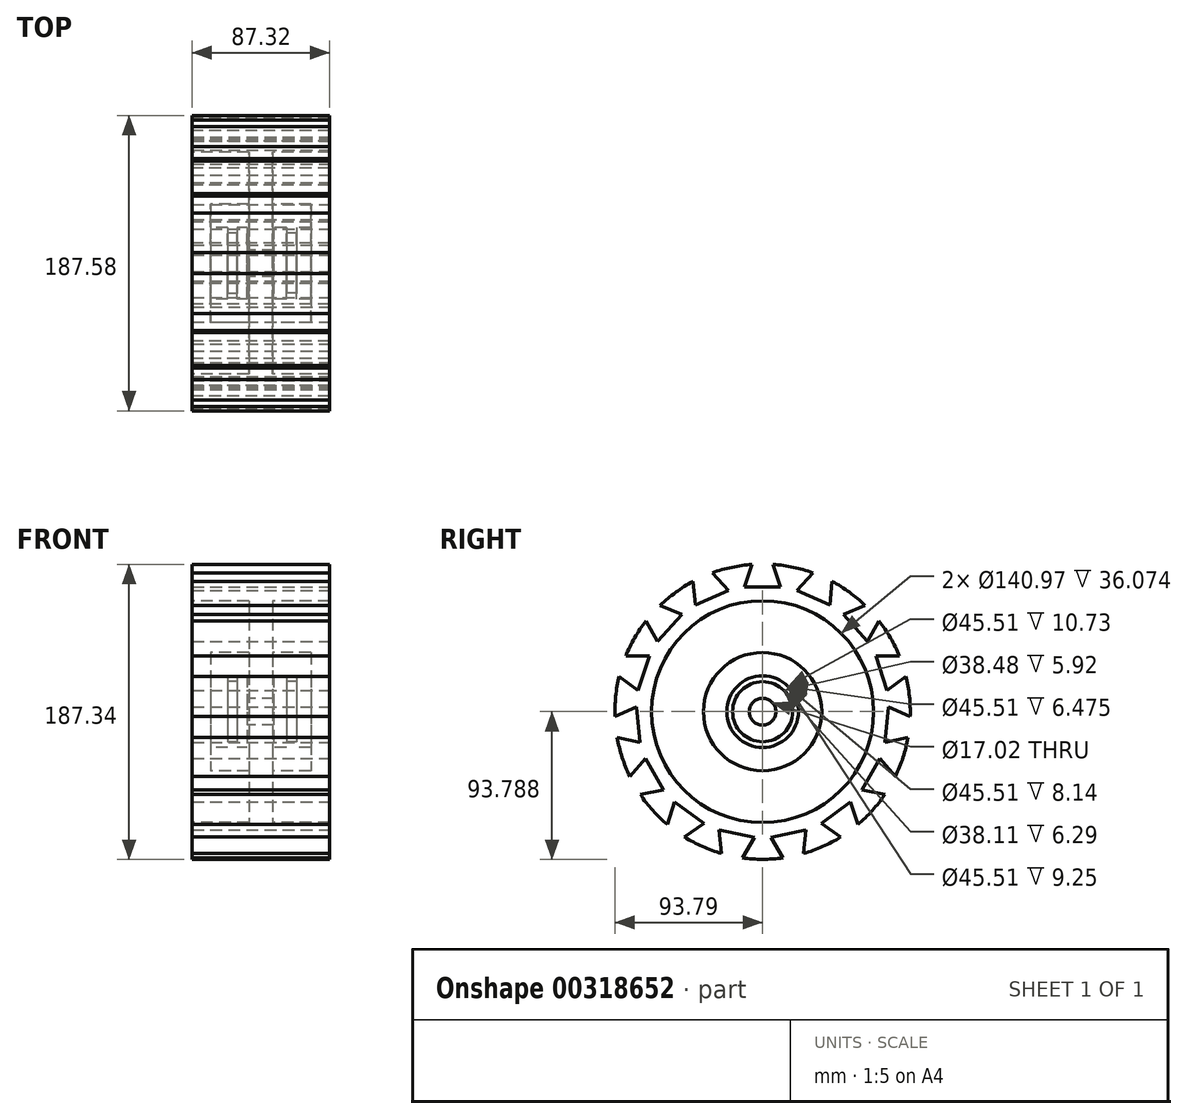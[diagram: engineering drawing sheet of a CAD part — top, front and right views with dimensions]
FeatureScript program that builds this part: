
annotation { "Feature Type Name" : "Feature", "Feature Type Description" : "" }
export const myFeature = defineFeature(function(context is Context, id is Id, definition is map)
    precondition{}
    {
        {
            var Q0;
            Q0=qCreatedBy(makeId("Front.planeOp"),FACE);
            var sketch = newSketch(context, id + "F0", { "sketchPlane" : qUnion([Q0])});
            skLineSegment(sketch, "E0.bottom", {"start": v(-43.66, 44.12) * mm, "end": v(-7.58, 44.12) * mm});
            skLineSegment(sketch, "E0.top", {"start": v(-43.66, 67.43) * mm, "end": v(43.66, 67.43) * mm});
            skLineSegment(sketch, "E0.left", {"start": v(-43.66, 44.12) * mm, "end": v(-43.66, 67.43) * mm});
            skLineSegment(sketch, "E0.right", {"start": v(43.66, 44.12) * mm, "end": v(43.66, 67.43) * mm});
            skPoint(sketch, "E0.middle", {"position": v(0, 55.78) * mm});
            skLineSegment(sketch, "E1.left", {"start": v(-7.58, 44.12) * mm, "end": v(-7.58, 11.2) * mm});
            skLineSegment(sketch, "E1.right", {"start": v(7.58, 44.12) * mm, "end": v(7.58, 11.2) * mm});
            skPoint(sketch, "E1.middle", {"position": v(0, 27.66) * mm});
            skLineSegment(sketch, "E2.bottom", {"start": v(-31.82, 11.2) * mm, "end": v(-7.58, 11.2) * mm});
            skLineSegment(sketch, "E2.top", {"start": v(-31.82, -3.6) * mm, "end": v(-21.09, -3.6) * mm});
            skLineSegment(sketch, "E2.left", {"start": v(-31.82, 11.2) * mm, "end": v(-31.82, -3.6) * mm});
            skLineSegment(sketch, "E2.right", {"start": v(31.82, 11.2) * mm, "end": v(31.82, -3.6) * mm});
            skPoint(sketch, "E2.middle", {"position": v(0, 3.8) * mm});
            skPoint(sketch, "E2.middle.positionSnap0", {"position": v(0, 11.2) * mm});
            skPoint(sketch, "E2.cornerSnap0", {"position": v(0, 11.2) * mm});
            skPoint(sketch, "E2.centerSnap0", {"position": v(0, 11.2) * mm});
            skLineSegment(sketch, "E3.top", {"start": v(-21.09, -7.12) * mm, "end": v(-15.17, -7.12) * mm});
            skLineSegment(sketch, "E3.left", {"start": v(-21.09, -3.6) * mm, "end": v(-21.09, -7.12) * mm});
            skLineSegment(sketch, "E3.right", {"start": v(-15.17, -3.6) * mm, "end": v(-15.17, -7.12) * mm});
            skLineSegment(sketch, "E4.top", {"start": v(16.28, -7.3) * mm, "end": v(22.57, -7.3) * mm});
            skLineSegment(sketch, "E4.left", {"start": v(16.28, -3.6) * mm, "end": v(16.28, -7.3) * mm});
            skLineSegment(sketch, "E4.right", {"start": v(22.57, -3.6) * mm, "end": v(22.57, -7.3) * mm});
            skLineSegment(sketch, "E5.top", {"start": v(-8.7, -17.85) * mm, "end": v(8.14, -17.85) * mm});
            skLineSegment(sketch, "E5.left", {"start": v(-8.7, -3.6) * mm, "end": v(-8.7, -17.85) * mm});
            skLineSegment(sketch, "E5.right", {"start": v(8.14, -3.6) * mm, "end": v(8.14, -17.85) * mm});
            skLineSegment(sketch, "E6.trimOffspring", {"start": v(22.57, -3.6) * mm, "end": v(31.82, -3.6) * mm});
            skLineSegment(sketch, "E7.trimOffspring", {"start": v(-15.17, -3.6) * mm, "end": v(-8.7, -3.6) * mm});
            skLineSegment(sketch, "E8.trimOffspring", {"start": v(7.58, 44.12) * mm, "end": v(43.66, 44.12) * mm});
            skLineSegment(sketch, "E9.trimOffspring", {"start": v(7.58, 11.2) * mm, "end": v(31.82, 11.2) * mm});
            skLineSegment(sketch, "E10.trimOffspring", {"start": v(8.14, -3.6) * mm, "end": v(16.28, -3.6) * mm});
            skLineSegment(sketch, "E11", {"start": v(-76.03, -26.36) * mm, "end": v(76.03, -26.36) * mm, "construction": true});
            skSolve(sketch);
        }
        {
            var Q0;
            Q0=makeQuery(id+"F0.imprint","IMPRINT",FACE,{"disambiguationData":[TD([[makeQuery(id+"F0.imprint","IMPRINT",EDGE,{"derivedFrom":sQuery(id+"F0.wireOp",EDGE,"E0.bottom")}),1.0]])]});
            var Q1;
            Q1=sQuery(id+"F0.wireOp",EDGE,"E11");
            revolve(context, id + "F1", {"entities" : qUnion([Q0]), "axis" : qUnion([Q1]), "revolveType" : RevolveType.FULL});
        }
        {
            var Q0;
            Q0=qCreatedBy(makeId("Right.planeOp"),FACE);
            var sketch = newSketch(context, id + "F2", { "sketchPlane" : qUnion([Q0])});
            skLineSegment(sketch, "E12", {"start": v(0, -21.86) * mm, "end": v(0, 75.63) * mm, "construction": true});
            skLineSegment(sketch, "E13", {"start": v(5.96, 69.43) * mm, "end": v(11.44, 52.98) * mm});
            skLineSegment(sketch, "E14.MirrorCS", {"start": v(-5.96, 69.43) * mm, "end": v(-11.44, 52.98) * mm});
            skLineSegment(sketch, "E15", {"start": v(-5.96, 69.43) * mm, "end": v(5.96, 69.43) * mm});
            skLineSegment(sketch, "E16", {"start": v(-11.44, 52.98) * mm, "end": v(11.44, 52.98) * mm});
            skSolve(sketch);
        }
        {
            var Q0;
            Q0=makeQuery(id+"F2.imprint","IMPRINT",FACE,{"disambiguationData":[TD([[makeQuery(id+"F2.imprint","IMPRINT",EDGE,{"derivedFrom":sQuery(id+"F2.wireOp",EDGE,"E13")}),-1.0]])]});
            extrude(context, id + "F3", {"entities" : qUnion([Q0]), "operationType" : NewBodyOperationType.REMOVE, "endBound" : BoundingType.SYMMETRIC, "oppositeDirection" : true, "depth" : 111.76 * mm});
        }
        {
            var Q0;
            Q0=makeQuery(id+"F3.boolean.opBoolean","COPY",FACE,{"derivedFrom":makeQuery(id+"F3.opExtrude","SWEPT_FACE",FACE,{"disambiguationData":[OSD([sQuery(id+"F2.wireOp",EDGE,"E16")])]})});
            var Q1;
            Q1=makeQuery(id+"F3.boolean.opBoolean","COPY",FACE,{"derivedFrom":makeQuery(id+"F3.opExtrude","SWEPT_FACE",FACE,{"disambiguationData":[OSD([sQuery(id+"F2.wireOp",EDGE,"E13")])]})});
            var Q2;
            Q2=makeQuery(id+"F3.boolean.opBoolean","COPY",FACE,{"derivedFrom":makeQuery(id+"F3.opExtrude","SWEPT_FACE",FACE,{"disambiguationData":[OSD([sQuery(id+"F2.wireOp",EDGE,"E14.MirrorCS")])]})});
            var Q3;
            Q3=makeQuery(id+"F1.opRevolve","SWEPT_EDGE",EDGE,{"disambiguationData":[OSD([sQuery(id+"F0.wireOp",EDGE,"E2.right"),sQuery(id+"F0.wireOp",EDGE,"E9.trimOffspring")])]});
            circularPattern(context, id + "F4", {"patternType" : PatternType.FACE, "faces" : qUnion([Q0, Q1, Q2]), "axis" : qUnion([Q3]), "angle" : 360 * degree, "instanceCount" : 15, "equalSpace" : true});
        }
    });
